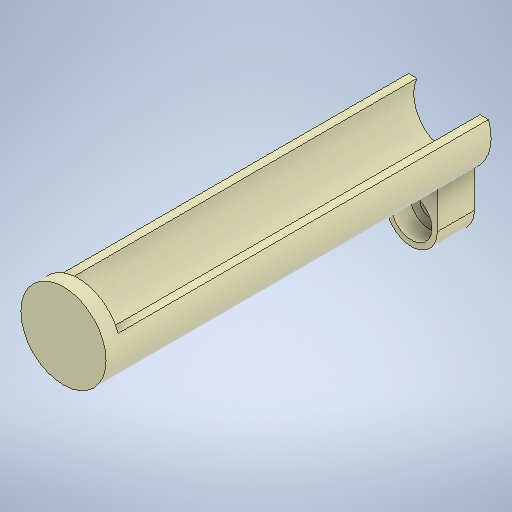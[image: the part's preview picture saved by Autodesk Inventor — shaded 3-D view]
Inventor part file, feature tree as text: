
AUTODESK INVENTOR PART (.ipt)
format: ipt  version: 2025.1 (Build 291241000, 241)  size: 285,696 bytes
history: native  units: mm
features: extrude x5, sketch x5
ambient origin geometry x8: Origin, YZ Plane, XZ Plane, XY Plane, X Axis, Y Axis, Z Axis, Center Point
bodies: Solid1 (feature_tree)
feature tree (10):
  extrude  "Extrusion1"  Depth=11.5mm
  extrude  "Extrusion2"  Depth=50.0mm TaperAngle=0.0deg
  extrude  "Extrusion3"  Depth=7.0mm
  extrude  "Extrusion4"  Depth=5.0mm TaperAngle=0.0deg
  extrude  "Extrusion5"  TaperAngle=0.0deg  [1 undecoded]
  sketch  "Sketch1"  dims[d0=9.4mm d1=11.5mm]
  sketch  "Sketch2"  dims[d2=2.0mm d3=50.0mm d4=0.0mm]
  sketch  "Sketch3"  dims[d5=2.0mm d6=0.0mm d7=7.0mm]
  sketch  "Sketch4"  dims[d9=5.0mm d10=5.0mm d11=0.0mm]
  sketch  "Sketch5"  dims[d12=2.7mm d13=0.0mm d14=0.0mm d15=5.5mm d16=2.5mm d17=0.0mm]
note: 1 required parameter value undecoded (feature->parameter linkage not recoverable at this tier; creation-order binding heuristic only, values carry confidence <= 0.55)
